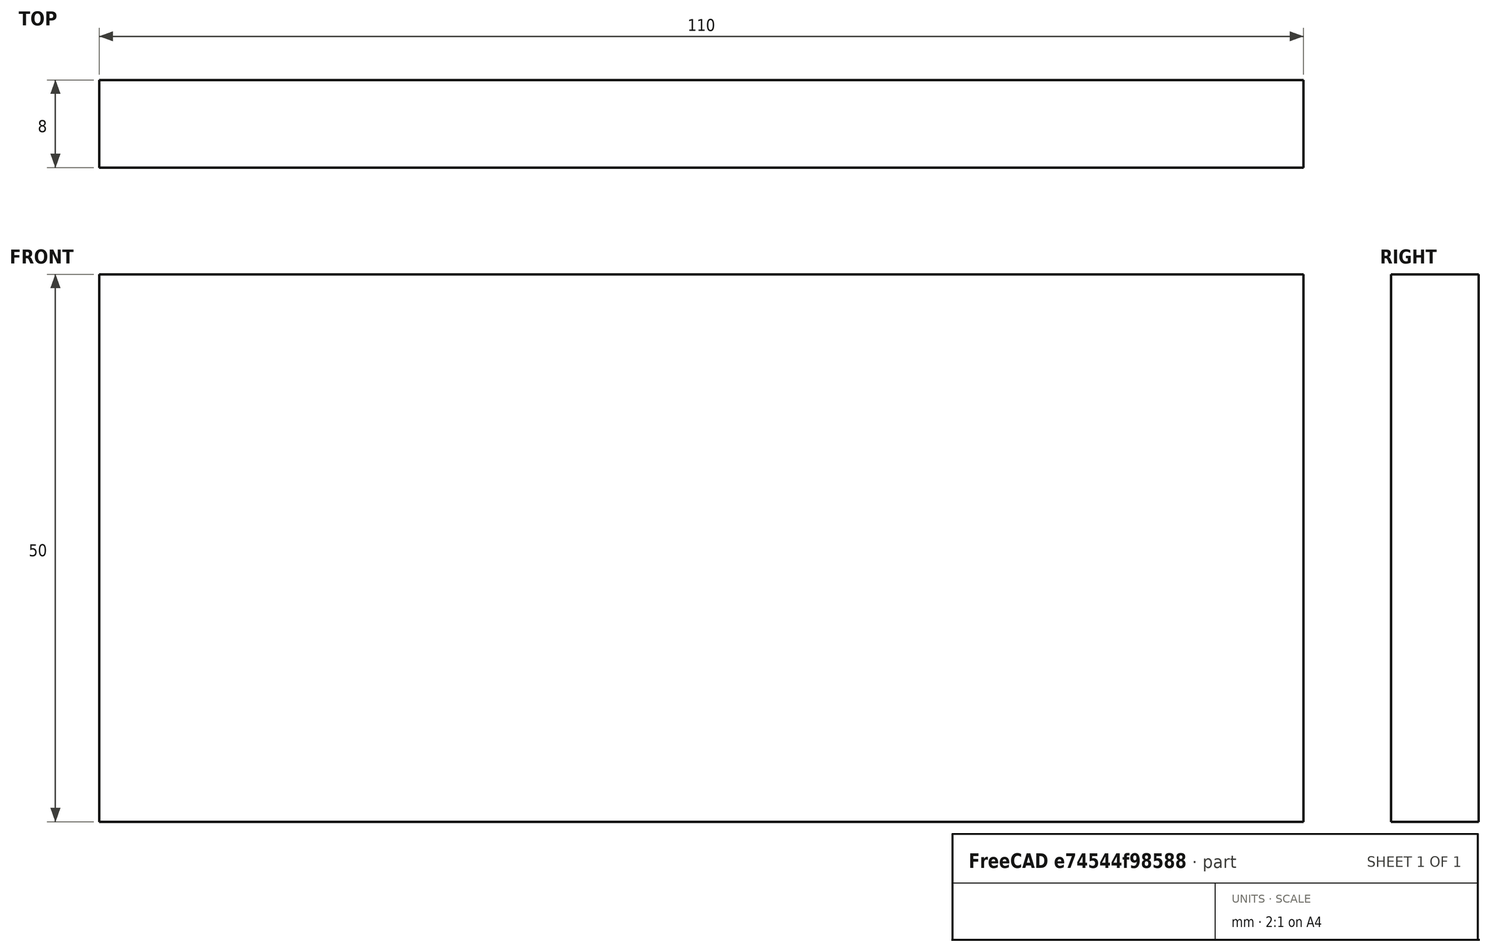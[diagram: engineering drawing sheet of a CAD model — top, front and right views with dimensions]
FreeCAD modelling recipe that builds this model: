
FCSTD DOCUMENT  (FreeCAD 0.15R4671 (Git))
Label: Flat Bar 110x8 EN10058 S235JR
License: All rights reserved
LicenseURL: http://en.wikipedia.org/wiki/All_rights_reserved
objects: Sketcher::SketchObject×1, Part::Extrusion×1
note: 2 computed .brp shape members not serialized (recipe doc carries the construction recipe); baked Part::Feature solids carry a one-line shape summary decoded from their .brp

FEATURE [Sketcher::SketchObject] Sketch
  sketch-geometry (4):
    g0: LineSegment StartX=-55 StartY=-4 StartZ=0 EndX=55 EndY=-4 EndZ=0
    g1: LineSegment StartX=55 StartY=-4 StartZ=0 EndX=55 EndY=4 EndZ=0
    g2: LineSegment StartX=55 StartY=4 StartZ=0 EndX=-55 EndY=4 EndZ=0
    g3: LineSegment StartX=-55 StartY=4 StartZ=0 EndX=-55 EndY=-4 EndZ=0
  constraints (12):
    c: Coincident(g0,g1)
    c: Coincident(g1,g2)
    c: Coincident(g2,g3)
    c: Coincident(g3,g0)
    c: Horizontal(g0)
    c: Horizontal(g2)
    c: Vertical(g1)
    c: Vertical(g3)
    c: Symmetric(g1,g2,g-2)
    c: Symmetric(g0,g1,g-1)
    c: DistanceY(g1) = 8
    c: DistanceX(g0) = 110
FEATURE [Part::Extrusion] Extrude  label="Flat Bar 110x8 EN10058 S235JR"
  Base = -> Sketch
  Dir = (0,0,50)
  Solid = true
